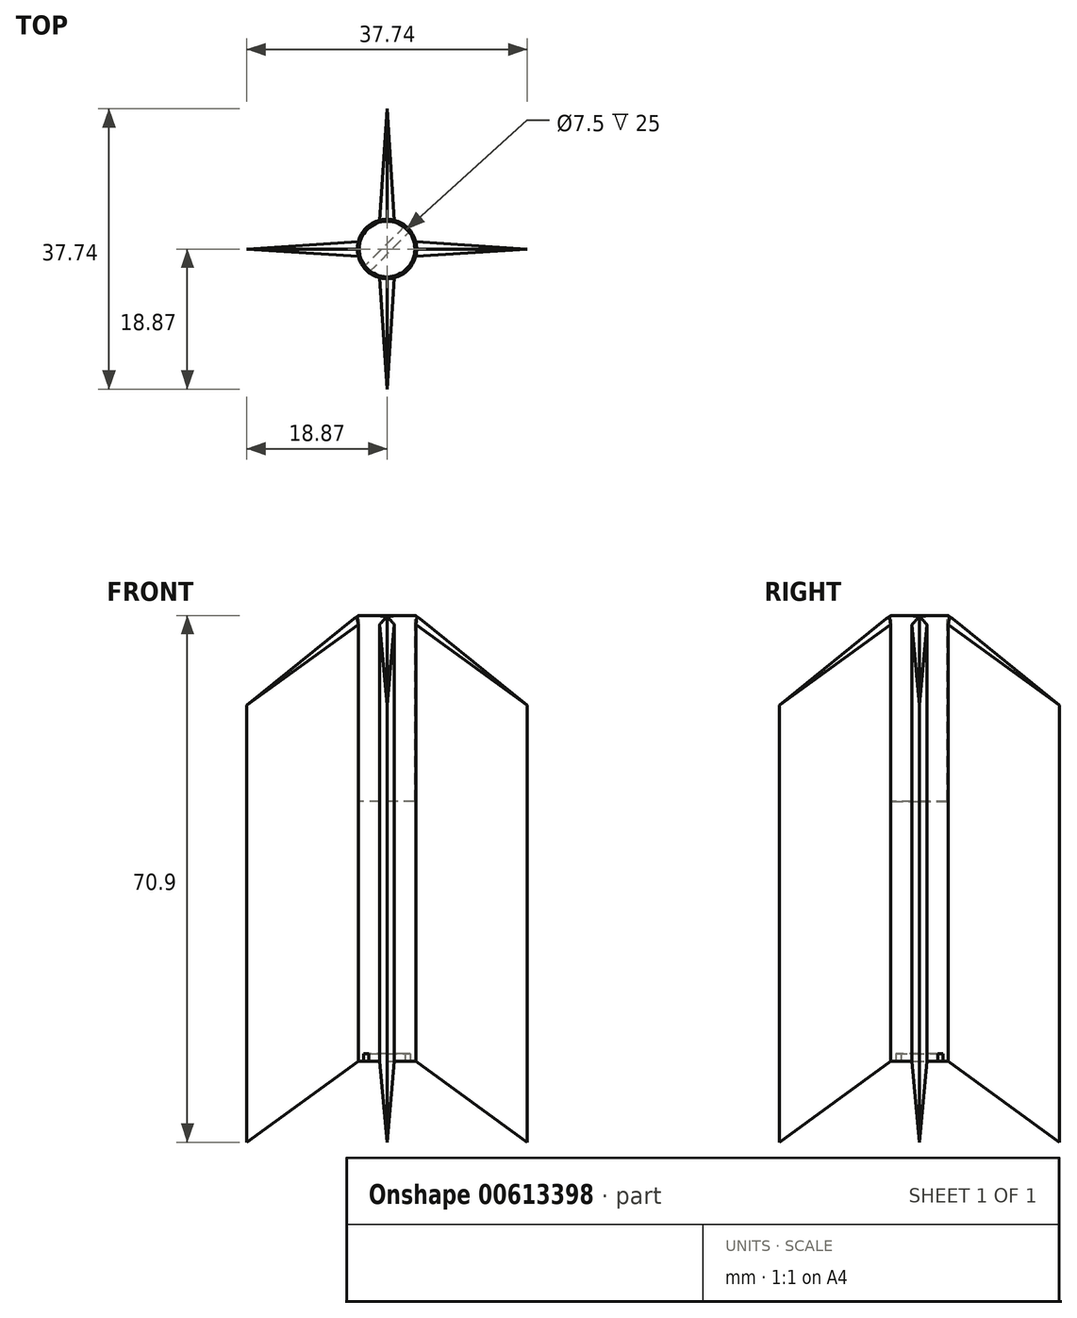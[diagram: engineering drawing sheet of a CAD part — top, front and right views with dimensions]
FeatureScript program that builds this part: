
annotation { "Feature Type Name" : "Feature", "Feature Type Description" : "" }
export const myFeature = defineFeature(function(context is Context, id is Id, definition is map)
    precondition{}
    {
        {
            var Q0;
            Q0=qCreatedBy(makeId("Top.planeOp"),FACE);
            var sketch = newSketch(context, id + "F0", { "sketchPlane" : qUnion([Q0])});
            skArc(sketch, "E0", {"start": v(-1, 3.87) * mm, "mid": v(-2.83, 2.83) * mm, "end": v(-3.87, 1) * mm});
            skLineSegment(sketch, "E1", {"start": v(-1, 3.87) * mm, "end": v(1, 3.87) * mm});
            skLineSegment(sketch, "E2", {"start": v(3.87, 1) * mm, "end": v(3.87, -1) * mm});
            skLineSegment(sketch, "E3", {"start": v(-1, -3.87) * mm, "end": v(1, -3.87) * mm});
            skLineSegment(sketch, "E4", {"start": v(-3.87, 1) * mm, "end": v(-3.87, -1) * mm});
            skArc(sketch, "E5.trimOffspring", {"start": v(3.87, 1) * mm, "mid": v(2.83, 2.83) * mm, "end": v(1, 3.87) * mm});
            skArc(sketch, "E6.trimOffspring", {"start": v(1, -3.87) * mm, "mid": v(2.83, -2.83) * mm, "end": v(3.87, -1) * mm});
            skArc(sketch, "E7.trimOffspring", {"start": v(-3.87, -1) * mm, "mid": v(-2.83, -2.83) * mm, "end": v(-1, -3.87) * mm});
            skSolve(sketch);
        }
        {
            var Q0;
            Q0=makeQuery(id+"F0.imprint","IMPRINT",FACE,{"disambiguationData":[TD([[makeQuery(id+"F0.imprint","IMPRINT",EDGE,{"derivedFrom":sQuery(id+"F0.wireOp",EDGE,"E0")}),1.0]])]});
            extrude(context, id + "F1", {"entities" : qUnion([Q0]), "depth" : 60 * mm, "offsetDistance" : 25 * mm});
        }
        {
            var Q0;
            Q0=makeQuery(id+"F1.opExtrude","SWEPT_FACE",FACE,{"disambiguationData":[OSD([sQuery(id+"F0.wireOp",EDGE,"E1")])]});
            var sketch = newSketch(context, id + "F2", { "sketchPlane" : qUnion([Q0])});
            skLineSegment(sketch, "E8.bottom", {"start": v(-1, 60) * mm, "end": v(1, 60) * mm});
            skLineSegment(sketch, "E8.top", {"start": v(-1, -40) * mm, "end": v(1, -40) * mm});
            skLineSegment(sketch, "E8.left", {"start": v(-1, 60) * mm, "end": v(-1, -40) * mm});
            skLineSegment(sketch, "E8.right", {"start": v(1, 60) * mm, "end": v(1, -40) * mm});
            skSolve(sketch);
        }
        {
            var Q0;
            {var subQ0=sQuery(id+"F2.wireOp",EDGE,"E8.bottom");Q0=makeQuery(id+"F2.imprint","IMPRINT",FACE,{"disambiguationData":[TD([[makeQuery(id+"F2.imprint","IMPRINT",EDGE,{"derivedFrom":subQ0}),1.0]])]});}
            var Q1;
            {var subQ0=sQuery(id+"F2.wireOp",EDGE,"E8.top");Q1=makeQuery(id+"F2.imprint","IMPRINT",FACE,{"disambiguationData":[TD([[makeQuery(id+"F2.imprint","IMPRINT",EDGE,{"derivedFrom":subQ0}),1.0]])]});}
            extrude(context, id + "F3", {"entities" : qUnion([Q0, Q1]), "operationType" : NewBodyOperationType.ADD, "depth" : 15 * mm, "offsetDistance" : 25 * mm});
        }
        {
            var Q0;
            Q0=makeQuery(id+"F3.opExtrude","SWEPT_FACE",FACE,{"disambiguationData":[OSD([sQuery(id+"F2.wireOp",EDGE,"E8.left")])]});
            var sketch = newSketch(context, id + "F4", { "sketchPlane" : qUnion([Q0])});
            skLineSegment(sketch, "E9", {"start": v(3.87, 60) * mm, "end": v(18.87, 49.1) * mm});
            skLineSegment(sketch, "E10", {"start": v(18.87, 49.1) * mm, "end": v(18.87, 60) * mm});
            skLineSegment(sketch, "E11", {"start": v(18.87, 60) * mm, "end": v(3.87, 60) * mm});
            skLineSegment(sketch, "E12", {"start": v(3.87, 0) * mm, "end": v(3.87, -40) * mm});
            skLineSegment(sketch, "E13", {"start": v(3.87, -40) * mm, "end": v(18.87, -40) * mm});
            skLineSegment(sketch, "E14", {"start": v(18.87, -10.9) * mm, "end": v(3.87, 0) * mm});
            skSolve(sketch);
        }
        {
            var Q0;
            Q0=makeQuery(id+"F4.imprint","IMPRINT",FACE,{"disambiguationData":[TD([[makeQuery(id+"F4.imprint","IMPRINT",EDGE,{"derivedFrom":sQuery(id+"F4.wireOp",EDGE,"E9")}),1.0]])]});
            var Q1;
            Q1=makeQuery(id+"F4.imprint","IMPRINT",FACE,{"disambiguationData":[TD([[makeQuery(id+"F4.imprint","IMPRINT",EDGE,{"derivedFrom":sQuery(id+"F4.wireOp",EDGE,"E12")}),1.0]])]});
            extrude(context, id + "F5", {"entities" : qUnion([Q0, Q1]), "operationType" : NewBodyOperationType.REMOVE, "oppositeDirection" : true, "depth" : 25 * mm, "offsetDistance" : 25 * mm});
        }
        {
            var Q0;
            Q0=makeQuery(id+"F1.opExtrude","SWEPT_FACE",FACE,{"disambiguationData":[OSD([sQuery(id+"F0.wireOp",EDGE,"E2")])]});
            var sketch = newSketch(context, id + "F6", { "sketchPlane" : qUnion([Q0])});
            skLineSegment(sketch, "E15.bottom", {"start": v(-1, 60) * mm, "end": v(1, 60) * mm});
            skLineSegment(sketch, "E15.top", {"start": v(-1, -40) * mm, "end": v(1, -40) * mm});
            skLineSegment(sketch, "E15.left", {"start": v(-1, 60) * mm, "end": v(-1, -40) * mm});
            skLineSegment(sketch, "E15.right", {"start": v(1, 60) * mm, "end": v(1, -40) * mm});
            skSolve(sketch);
        }
        {
            var Q0;
            {var subQ0=sQuery(id+"F6.wireOp",EDGE,"E15.top");Q0=makeQuery(id+"F6.imprint","IMPRINT",FACE,{"disambiguationData":[TD([[makeQuery(id+"F6.imprint","IMPRINT",EDGE,{"derivedFrom":subQ0}),1.0]])]});}
            var Q1;
            {var subQ0=sQuery(id+"F6.wireOp",EDGE,"E15.bottom");Q1=makeQuery(id+"F6.imprint","IMPRINT",FACE,{"disambiguationData":[TD([[makeQuery(id+"F6.imprint","IMPRINT",EDGE,{"derivedFrom":subQ0}),1.0]])]});}
            extrude(context, id + "F7", {"entities" : qUnion([Q0, Q1]), "operationType" : NewBodyOperationType.ADD, "depth" : 15 * mm, "offsetDistance" : 25 * mm});
        }
        {
            var Q0;
            Q0=makeQuery(id+"F7.opExtrude","SWEPT_FACE",FACE,{"disambiguationData":[OSD([sQuery(id+"F6.wireOp",EDGE,"E15.right")])]});
            var sketch = newSketch(context, id + "F8", { "sketchPlane" : qUnion([Q0])});
            skLineSegment(sketch, "E16", {"start": v(-3.87, 60) * mm, "end": v(-18.87, 60) * mm});
            skLineSegment(sketch, "E17", {"start": v(-3.87, 60) * mm, "end": v(-18.87, 49.1) * mm});
            skLineSegment(sketch, "E18", {"start": v(-18.87, 49.1) * mm, "end": v(-18.87, 60) * mm});
            skLineSegment(sketch, "E19", {"start": v(-3.87, 0) * mm, "end": v(-3.87, -40) * mm});
            skLineSegment(sketch, "E20", {"start": v(-3.87, -40) * mm, "end": v(-18.87, -40) * mm});
            skLineSegment(sketch, "E21", {"start": v(-18.87, -40) * mm, "end": v(-18.87, -10.9) * mm});
            skLineSegment(sketch, "E22", {"start": v(-18.87, -10.9) * mm, "end": v(-3.87, 0) * mm});
            skLineSegment(sketch, "E23", {"start": v(-18.87, -10.9) * mm, "end": v(-18.87, 49.1) * mm});
            skSolve(sketch);
        }
        {
            var Q0;
            Q0 = qSketchRegion(id + "F8", true);
            extrude(context, id + "F9", {"entities" : qUnion([Q0]), "operationType" : NewBodyOperationType.REMOVE, "oppositeDirection" : true, "depth" : 25 * mm, "offsetDistance" : 25 * mm});
        }
        {
            var Q0;
            Q0=makeQuery(id+"F1.opExtrude","SWEPT_FACE",FACE,{"disambiguationData":[OSD([sQuery(id+"F0.wireOp",EDGE,"E3")])]});
            var sketch = newSketch(context, id + "F10", { "sketchPlane" : qUnion([Q0])});
            skLineSegment(sketch, "E24.bottom", {"start": v(-1, 60) * mm, "end": v(1, 60) * mm});
            skLineSegment(sketch, "E24.top", {"start": v(-1, -40) * mm, "end": v(1, -40) * mm});
            skLineSegment(sketch, "E24.left", {"start": v(-1, 60) * mm, "end": v(-1, -40) * mm});
            skLineSegment(sketch, "E24.right", {"start": v(1, 60) * mm, "end": v(1, -40) * mm});
            skSolve(sketch);
        }
        {
            var Q0;
            {var subQ0=sQuery(id+"F10.wireOp",EDGE,"E24.bottom");Q0=makeQuery(id+"F10.imprint","IMPRINT",FACE,{"disambiguationData":[TD([[makeQuery(id+"F10.imprint","IMPRINT",EDGE,{"derivedFrom":subQ0}),-1.0]])]});}
            var Q1;
            {var subQ0=sQuery(id+"F10.wireOp",EDGE,"E24.top");Q1=makeQuery(id+"F10.imprint","IMPRINT",FACE,{"disambiguationData":[TD([[makeQuery(id+"F10.imprint","IMPRINT",EDGE,{"derivedFrom":subQ0}),1.0]])]});}
            extrude(context, id + "F11", {"entities" : qUnion([Q0, Q1]), "operationType" : NewBodyOperationType.ADD, "depth" : 15 * mm, "offsetDistance" : 25 * mm});
        }
        {
            var Q0;
            Q0=makeQuery(id+"F11.opExtrude","SWEPT_FACE",FACE,{"disambiguationData":[OSD([sQuery(id+"F10.wireOp",EDGE,"E24.right")])]});
            var sketch = newSketch(context, id + "F12", { "sketchPlane" : qUnion([Q0])});
            skLineSegment(sketch, "E25", {"start": v(-3.87, 60) * mm, "end": v(-18.87, 60) * mm});
            skLineSegment(sketch, "E26", {"start": v(-18.87, 60) * mm, "end": v(-18.87, 49.1) * mm});
            skLineSegment(sketch, "E27", {"start": v(-18.87, 49.1) * mm, "end": v(-3.87, 60) * mm});
            skLineSegment(sketch, "E28", {"start": v(-18.87, -40) * mm, "end": v(-18.87, -10.9) * mm});
            skLineSegment(sketch, "E29", {"start": v(-18.87, -10.9) * mm, "end": v(-3.87, 0) * mm});
            skLineSegment(sketch, "E30", {"start": v(-3.87, 0) * mm, "end": v(-3.87, -40) * mm});
            skLineSegment(sketch, "E31", {"start": v(-3.87, -40) * mm, "end": v(-18.87, -40) * mm});
            skSolve(sketch);
        }
        {
            var Q0;
            Q0=makeQuery(id+"F12.imprint","IMPRINT",FACE,{"disambiguationData":[TD([[makeQuery(id+"F12.imprint","IMPRINT",EDGE,{"derivedFrom":sQuery(id+"F12.wireOp",EDGE,"E28")}),1.0]])]});
            var Q1;
            Q1=makeQuery(id+"F12.imprint","IMPRINT",FACE,{"disambiguationData":[TD([[makeQuery(id+"F12.imprint","IMPRINT",EDGE,{"derivedFrom":sQuery(id+"F12.wireOp",EDGE,"E25")}),-1.0]])]});
            extrude(context, id + "F13", {"entities" : qUnion([Q0, Q1]), "operationType" : NewBodyOperationType.REMOVE, "oppositeDirection" : true, "depth" : 25 * mm, "offsetDistance" : 25 * mm});
        }
        {
            var Q0;
            Q0=makeQuery(id+"F1.opExtrude","SWEPT_FACE",FACE,{"disambiguationData":[OSD([sQuery(id+"F0.wireOp",EDGE,"E4")])]});
            var sketch = newSketch(context, id + "F14", { "sketchPlane" : qUnion([Q0])});
            skLineSegment(sketch, "E32.bottom", {"start": v(1, 60) * mm, "end": v(-1, 60) * mm});
            skLineSegment(sketch, "E32.top", {"start": v(1, -40) * mm, "end": v(-1, -40) * mm});
            skLineSegment(sketch, "E32.left", {"start": v(1, 60) * mm, "end": v(1, -40) * mm});
            skLineSegment(sketch, "E32.right", {"start": v(-1, 60) * mm, "end": v(-1, -40) * mm});
            skSolve(sketch);
        }
        {
            var Q0;
            {var subQ0=sQuery(id+"F14.wireOp",EDGE,"E32.top");Q0=makeQuery(id+"F14.imprint","IMPRINT",FACE,{"disambiguationData":[TD([[makeQuery(id+"F14.imprint","IMPRINT",EDGE,{"derivedFrom":subQ0}),-1.0]])]});}
            var Q1;
            {var subQ0=sQuery(id+"F14.wireOp",EDGE,"E32.bottom");Q1=makeQuery(id+"F14.imprint","IMPRINT",FACE,{"disambiguationData":[TD([[makeQuery(id+"F14.imprint","IMPRINT",EDGE,{"derivedFrom":subQ0}),-1.0]])]});}
            extrude(context, id + "F15", {"entities" : qUnion([Q0, Q1]), "operationType" : NewBodyOperationType.ADD, "depth" : 15 * mm, "offsetDistance" : 25 * mm});
        }
        {
            var Q0;
            Q0=makeQuery(id+"F15.opExtrude","SWEPT_FACE",FACE,{"disambiguationData":[OSD([sQuery(id+"F14.wireOp",EDGE,"E32.left")])]});
            var sketch = newSketch(context, id + "F16", { "sketchPlane" : qUnion([Q0])});
            skLineSegment(sketch, "E33", {"start": v(-3.87, 60) * mm, "end": v(-18.87, 60) * mm});
            skLineSegment(sketch, "E34", {"start": v(-18.87, 60) * mm, "end": v(-18.87, 49.1) * mm});
            skLineSegment(sketch, "E35", {"start": v(-18.87, 49.1) * mm, "end": v(-3.87, 60) * mm});
            skLineSegment(sketch, "E36", {"start": v(-18.87, -40) * mm, "end": v(-18.87, -10.9) * mm});
            skLineSegment(sketch, "E37", {"start": v(-18.87, -10.9) * mm, "end": v(-3.87, 0) * mm});
            skLineSegment(sketch, "E38", {"start": v(-3.87, 0) * mm, "end": v(-3.87, -40) * mm});
            skLineSegment(sketch, "E39", {"start": v(-3.87, -40) * mm, "end": v(-18.87, -40) * mm});
            skSolve(sketch);
        }
        {
            var Q0;
            Q0=makeQuery(id+"F16.imprint","IMPRINT",FACE,{"disambiguationData":[TD([[makeQuery(id+"F16.imprint","IMPRINT",EDGE,{"derivedFrom":sQuery(id+"F16.wireOp",EDGE,"E36")}),1.0]])]});
            var Q1;
            Q1=makeQuery(id+"F16.imprint","IMPRINT",FACE,{"disambiguationData":[TD([[makeQuery(id+"F16.imprint","IMPRINT",EDGE,{"derivedFrom":sQuery(id+"F16.wireOp",EDGE,"E33")}),-1.0]])]});
            extrude(context, id + "F17", {"entities" : qUnion([Q0, Q1]), "operationType" : NewBodyOperationType.REMOVE, "oppositeDirection" : true, "depth" : 25 * mm, "offsetDistance" : 25 * mm});
        }
        {
            var Q0;
            Q0=makeQuery(id+"F3.opExtrude","CAP_EDGE",EDGE,{"disambiguationData":[OSD([sQuery(id+"F2.wireOp",EDGE,"E8.left")])],"isStart":false});
            var Q1;
            Q1=makeQuery(id+"F15.opExtrude","CAP_EDGE",EDGE,{"disambiguationData":[OSD([sQuery(id+"F14.wireOp",EDGE,"E32.right")])],"isStart":false});
            var Q2;
            Q2=makeQuery(id+"F7.opExtrude","CAP_EDGE",EDGE,{"disambiguationData":[OSD([sQuery(id+"F6.wireOp",EDGE,"E15.left")])],"isStart":false});
            var Q3;
            Q3=makeQuery(id+"F11.opExtrude","CAP_EDGE",EDGE,{"disambiguationData":[OSD([sQuery(id+"F10.wireOp",EDGE,"E24.left")])],"isStart":false});
            chamfer(context, id + "F18", {"entities" : qUnion([Q0, Q1, Q2, Q3]), "chamferType" : ChamferType.TWO_OFFSETS, "width1" : 1 * mm, "oppositeDirection" : false, "width2" : 15 * mm, "tangentPropagation" : true});
        }
        {
            var Q0;
            Q0=makeQuery(id+"F3.opExtrude","CAP_EDGE",EDGE,{"disambiguationData":[OSD([sQuery(id+"F2.wireOp",EDGE,"E8.right")])],"isStart":false});
            var Q1;
            Q1=makeQuery(id+"F15.opExtrude","CAP_EDGE",EDGE,{"disambiguationData":[OSD([sQuery(id+"F14.wireOp",EDGE,"E32.left")])],"isStart":false});
            var Q2;
            Q2=makeQuery(id+"F11.opExtrude","CAP_EDGE",EDGE,{"disambiguationData":[OSD([sQuery(id+"F10.wireOp",EDGE,"E24.right")])],"isStart":false});
            var Q3;
            Q3=makeQuery(id+"F7.opExtrude","CAP_EDGE",EDGE,{"disambiguationData":[OSD([sQuery(id+"F6.wireOp",EDGE,"E15.right")])],"isStart":false});
            chamfer(context, id + "F19", {"entities" : qUnion([Q0, Q1, Q2, Q3]), "chamferType" : ChamferType.TWO_OFFSETS, "width1" : 15 * mm, "oppositeDirection" : false, "width2" : 1 * mm, "tangentPropagation" : true});
        }
        {
            var Q0;
            Q0=makeQuery(id+"F15.boolean.opBoolean","MERGE",FACE,{"derivedFrom":[makeQuery(id+"F11.boolean.opBoolean","MERGE",FACE,{"derivedFrom":[makeQuery(id+"F7.boolean.opBoolean","MERGE",FACE,{"derivedFrom":[makeQuery(id+"F3.boolean.opBoolean","MERGE",FACE,{"derivedFrom":[makeQuery(id+"F1.opExtrude","CAP_FACE",FACE,{"disambiguationData":[OSD([sQuery(id+"F0.wireOp",EDGE,"E0"),sQuery(id+"F0.wireOp",EDGE,"E1"),sQuery(id+"F0.wireOp",EDGE,"E2"),sQuery(id+"F0.wireOp",EDGE,"E3"),sQuery(id+"F0.wireOp",EDGE,"E4"),sQuery(id+"F0.wireOp",EDGE,"E5.trimOffspring"),sQuery(id+"F0.wireOp",EDGE,"E6.trimOffspring"),sQuery(id+"F0.wireOp",EDGE,"E7.trimOffspring")])],"isStart":false}),makeQuery(id+"F3.opExtrude","SWEPT_FACE",FACE,{"disambiguationData":[OSD([sQuery(id+"F2.wireOp",EDGE,"E8.bottom")])]})]}),makeQuery(id+"F7.opExtrude","SWEPT_FACE",FACE,{"disambiguationData":[OSD([sQuery(id+"F6.wireOp",EDGE,"E15.bottom")])]})]}),makeQuery(id+"F11.opExtrude","SWEPT_FACE",FACE,{"disambiguationData":[OSD([sQuery(id+"F10.wireOp",EDGE,"E24.bottom")])]})]}),makeQuery(id+"F15.opExtrude","SWEPT_FACE",FACE,{"disambiguationData":[OSD([sQuery(id+"F14.wireOp",EDGE,"E32.bottom")])]})]});
            var sketch = newSketch(context, id + "F20", { "sketchPlane" : qUnion([Q0])});
            skCircle(sketch, "E40", {"center": v(0, 0) * mm, "radius": 3.75 * mm});
            skSolve(sketch);
        }
        {
            var Q0;
            Q0=makeQuery(id+"F20.imprint","IMPRINT",FACE,{"disambiguationData":[TD([[makeQuery(id+"F20.imprint","IMPRINT",EDGE,{"derivedFrom":sQuery(id+"F20.wireOp",EDGE,"E40")}),1.0]])]});
            extrude(context, id + "F21", {"entities" : qUnion([Q0]), "operationType" : NewBodyOperationType.REMOVE, "oppositeDirection" : true, "depth" : 25 * mm, "offsetDistance" : 25 * mm});
        }
        {
            var Q0;
            Q0=makeQuery(id+"F18.opChamfer","BLEND_EDGE",EDGE,{"blendedFrom":[makeQuery(id+"F3.opExtrude","CAP_EDGE",EDGE,{"disambiguationData":[OSD([sQuery(id+"F2.wireOp",EDGE,"E8.left")])],"isStart":false}),makeQuery(id+"F5.boolean.opBoolean","COPY",FACE,{"derivedFrom":makeQuery(id+"F5.opExtrude","SWEPT_FACE",FACE,{"disambiguationData":[OSD([sQuery(id+"F4.wireOp",EDGE,"E9")])]})})],"blendedInto":[makeQuery(id+"F5.boolean.opBoolean","COPY",FACE,{"derivedFrom":makeQuery(id+"F5.opExtrude","SWEPT_FACE",FACE,{"disambiguationData":[OSD([sQuery(id+"F4.wireOp",EDGE,"E9")])]})})]});
            var Q1;
            Q1=makeQuery(id+"F18.opChamfer","BLEND_EDGE",EDGE,{"blendedFrom":[makeQuery(id+"F15.opExtrude","CAP_EDGE",EDGE,{"disambiguationData":[OSD([sQuery(id+"F14.wireOp",EDGE,"E32.right")])],"isStart":false}),makeQuery(id+"F17.boolean.opBoolean","COPY",FACE,{"derivedFrom":makeQuery(id+"F17.opExtrude","SWEPT_FACE",FACE,{"disambiguationData":[OSD([sQuery(id+"F16.wireOp",EDGE,"E35")])]})})],"blendedInto":[makeQuery(id+"F17.boolean.opBoolean","COPY",FACE,{"derivedFrom":makeQuery(id+"F17.opExtrude","SWEPT_FACE",FACE,{"disambiguationData":[OSD([sQuery(id+"F16.wireOp",EDGE,"E35")])]})})]});
            var Q2;
            Q2=makeQuery(id+"F18.opChamfer","BLEND_EDGE",EDGE,{"blendedFrom":[makeQuery(id+"F11.opExtrude","CAP_EDGE",EDGE,{"disambiguationData":[OSD([sQuery(id+"F10.wireOp",EDGE,"E24.left")])],"isStart":false}),makeQuery(id+"F13.boolean.opBoolean","COPY",FACE,{"derivedFrom":makeQuery(id+"F13.opExtrude","SWEPT_FACE",FACE,{"disambiguationData":[OSD([sQuery(id+"F12.wireOp",EDGE,"E27")])]})})],"blendedInto":[makeQuery(id+"F13.boolean.opBoolean","COPY",FACE,{"derivedFrom":makeQuery(id+"F13.opExtrude","SWEPT_FACE",FACE,{"disambiguationData":[OSD([sQuery(id+"F12.wireOp",EDGE,"E27")])]})})]});
            var Q3;
            Q3=makeQuery(id+"F18.opChamfer","BLEND_EDGE",EDGE,{"blendedFrom":[makeQuery(id+"F7.opExtrude","CAP_EDGE",EDGE,{"disambiguationData":[OSD([sQuery(id+"F6.wireOp",EDGE,"E15.left")])],"isStart":false}),makeQuery(id+"F9.boolean.opBoolean","COPY",FACE,{"derivedFrom":makeQuery(id+"F9.opExtrude","SWEPT_FACE",FACE,{"disambiguationData":[OSD([sQuery(id+"F8.wireOp",EDGE,"E17")])]})})],"blendedInto":[makeQuery(id+"F9.boolean.opBoolean","COPY",FACE,{"derivedFrom":makeQuery(id+"F9.opExtrude","SWEPT_FACE",FACE,{"disambiguationData":[OSD([sQuery(id+"F8.wireOp",EDGE,"E17")])]})})]});
            chamfer(context, id + "F22", {"entities" : qUnion([Q0, Q1, Q2, Q3]), "width" : 1 * mm, "tangentPropagation" : true});
        }
        {
            var Q0;
            Q0=makeQuery(id+"F19.opChamfer","BLEND_EDGE",EDGE,{"blendedFrom":[makeQuery(id+"F7.opExtrude","CAP_EDGE",EDGE,{"disambiguationData":[OSD([sQuery(id+"F6.wireOp",EDGE,"E15.right")])],"isStart":false}),makeQuery(id+"F9.boolean.opBoolean","COPY",FACE,{"derivedFrom":makeQuery(id+"F9.opExtrude","SWEPT_FACE",FACE,{"disambiguationData":[OSD([sQuery(id+"F8.wireOp",EDGE,"E17")])]})})],"blendedInto":[makeQuery(id+"F9.boolean.opBoolean","COPY",FACE,{"derivedFrom":makeQuery(id+"F9.opExtrude","SWEPT_FACE",FACE,{"disambiguationData":[OSD([sQuery(id+"F8.wireOp",EDGE,"E17")])]})})]});
            var Q1;
            Q1=makeQuery(id+"F19.opChamfer","BLEND_EDGE",EDGE,{"blendedFrom":[makeQuery(id+"F3.opExtrude","CAP_EDGE",EDGE,{"disambiguationData":[OSD([sQuery(id+"F2.wireOp",EDGE,"E8.right")])],"isStart":false}),makeQuery(id+"F5.boolean.opBoolean","COPY",FACE,{"derivedFrom":makeQuery(id+"F5.opExtrude","SWEPT_FACE",FACE,{"disambiguationData":[OSD([sQuery(id+"F4.wireOp",EDGE,"E9")])]})})],"blendedInto":[makeQuery(id+"F5.boolean.opBoolean","COPY",FACE,{"derivedFrom":makeQuery(id+"F5.opExtrude","SWEPT_FACE",FACE,{"disambiguationData":[OSD([sQuery(id+"F4.wireOp",EDGE,"E9")])]})})]});
            var Q2;
            Q2=makeQuery(id+"F19.opChamfer","BLEND_EDGE",EDGE,{"blendedFrom":[makeQuery(id+"F15.opExtrude","CAP_EDGE",EDGE,{"disambiguationData":[OSD([sQuery(id+"F14.wireOp",EDGE,"E32.left")])],"isStart":false}),makeQuery(id+"F17.boolean.opBoolean","COPY",FACE,{"derivedFrom":makeQuery(id+"F17.opExtrude","SWEPT_FACE",FACE,{"disambiguationData":[OSD([sQuery(id+"F16.wireOp",EDGE,"E35")])]})})],"blendedInto":[makeQuery(id+"F17.boolean.opBoolean","COPY",FACE,{"derivedFrom":makeQuery(id+"F17.opExtrude","SWEPT_FACE",FACE,{"disambiguationData":[OSD([sQuery(id+"F16.wireOp",EDGE,"E35")])]})})]});
            var Q3;
            Q3=makeQuery(id+"F19.opChamfer","BLEND_EDGE",EDGE,{"blendedFrom":[makeQuery(id+"F11.opExtrude","CAP_EDGE",EDGE,{"disambiguationData":[OSD([sQuery(id+"F10.wireOp",EDGE,"E24.right")])],"isStart":false}),makeQuery(id+"F13.boolean.opBoolean","COPY",FACE,{"derivedFrom":makeQuery(id+"F13.opExtrude","SWEPT_FACE",FACE,{"disambiguationData":[OSD([sQuery(id+"F12.wireOp",EDGE,"E27")])]})})],"blendedInto":[makeQuery(id+"F13.boolean.opBoolean","COPY",FACE,{"derivedFrom":makeQuery(id+"F13.opExtrude","SWEPT_FACE",FACE,{"disambiguationData":[OSD([sQuery(id+"F12.wireOp",EDGE,"E27")])]})})]});
            chamfer(context, id + "F23", {"entities" : qUnion([Q0, Q1, Q2, Q3]), "width" : 1 * mm, "tangentPropagation" : true});
        }
        {
            var Q0;
            Q0=makeQuery(id+"F1.opExtrude","CAP_FACE",FACE,{"disambiguationData":[OSD([sQuery(id+"F0.wireOp",EDGE,"E0"),sQuery(id+"F0.wireOp",EDGE,"E1"),sQuery(id+"F0.wireOp",EDGE,"E2"),sQuery(id+"F0.wireOp",EDGE,"E3"),sQuery(id+"F0.wireOp",EDGE,"E4"),sQuery(id+"F0.wireOp",EDGE,"E5.trimOffspring"),sQuery(id+"F0.wireOp",EDGE,"E6.trimOffspring"),sQuery(id+"F0.wireOp",EDGE,"E7.trimOffspring")])],"isStart":true});
            var sketch = newSketch(context, id + "F24", { "sketchPlane" : qUnion([Q0])});
            skLineSegment(sketch, "E41", {"start": v(-2.83, 2.83) * mm, "end": v(2.83, -2.83) * mm});
            skLineSegment(sketch, "E42", {"start": v(-2.47, 3.18) * mm, "end": v(-3.18, 2.47) * mm});
            skLineSegment(sketch, "E43", {"start": v(-2.47, 3.18) * mm, "end": v(3.18, -2.47) * mm});
            skLineSegment(sketch, "E44", {"start": v(3.18, -2.47) * mm, "end": v(2.47, -3.18) * mm});
            skLineSegment(sketch, "E45", {"start": v(2.47, -3.18) * mm, "end": v(-3.18, 2.47) * mm});
            skSolve(sketch);
        }
        {
            var Q0;
            {var subQ0=sQuery(id+"F24.wireOp",EDGE,"E41");Q0=makeQuery(id+"F24.imprint","IMPRINT",FACE,{"disambiguationData":[TD([[makeQuery(id+"F24.imprint","IMPRINT",EDGE,{"derivedFrom":subQ0}),-1.0]])]});}
            var Q1;
            {var subQ0=sQuery(id+"F24.wireOp",EDGE,"E41");Q1=makeQuery(id+"F24.imprint","IMPRINT",FACE,{"disambiguationData":[TD([[makeQuery(id+"F24.imprint","IMPRINT",EDGE,{"derivedFrom":subQ0}),1.0]])]});}
            extrude(context, id + "F25", {"entities" : qUnion([Q0, Q1]), "operationType" : NewBodyOperationType.REMOVE, "oppositeDirection" : true, "depth" : 1 * mm, "offsetDistance" : 25 * mm});
        }
    });
